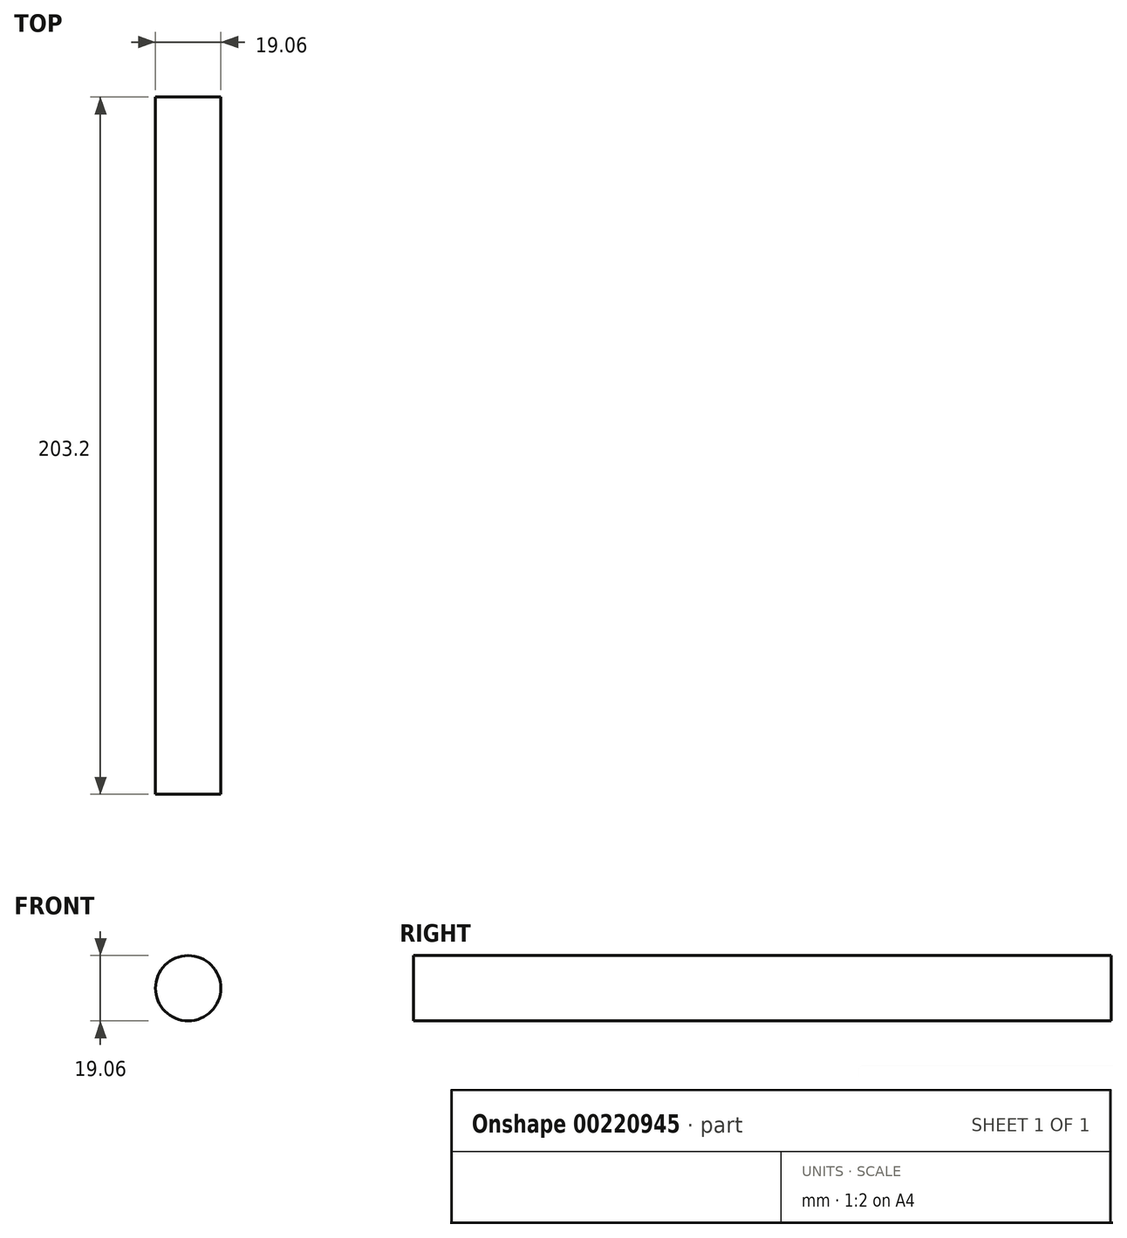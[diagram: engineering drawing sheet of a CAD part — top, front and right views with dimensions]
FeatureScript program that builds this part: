
annotation { "Feature Type Name" : "Feature", "Feature Type Description" : "" }
export const myFeature = defineFeature(function(context is Context, id is Id, definition is map)
    precondition{}
    {
        {
            var Q0;
            Q0=qCreatedBy(makeId("Front.planeOp"),FACE);
            var sketch = newSketch(context, id + "F0", { "sketchPlane" : qUnion([Q0])});
            skCircle(sketch, "E0", {"center": v(0, 0) * mm, "radius": 9.53 * mm});
            skSolve(sketch);
        }
        {
            var Q0;
            Q0 = qSketchRegion(id + "F0", true);
            extrude(context, id + "F1", {"entities" : qUnion([Q0]), "depth" : 203.2 * mm});
        }
    });
